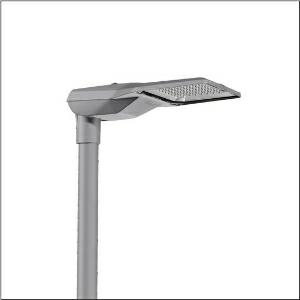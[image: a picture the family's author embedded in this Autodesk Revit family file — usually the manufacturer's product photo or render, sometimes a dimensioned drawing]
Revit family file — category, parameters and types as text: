
# Revit family: streetlight_sl_21_midi___st1_5a_5xe3p33s08mb_c1a7
name_source: partatom
category: Lighting Fixtures
units: mm (PartAtom-declared; Revit-internal decimal feet)

## family parameters
Cut with Voids When Loaded = No
Host = Face
Light Source = No
Part Type = Normal
Room Calculation Point = No
Round Connector Dimension = Use Diameter
Shared = No

## types (1)
- --- (1 x LED, 17960 lm, 136 W, 3000K)
    Apparent Load = 136 VA
    CIE Flux Codes = 22 53 95 100 100
    Color Rendering = 70
    Color Temperature = 3000K
    Default Elevation = 1800 mm
    Description = Streetlight SL 21 midi, mast luminaire, primary light control with lens, of PMMA, primary optical cover: cover, of toughened safety glass, transparent, light distribution: ST1.5a, light emission: direct distribution, primary light characteristic: asymmetric, installation type: side-entry, post-top, LED, High Power LED, rated luminous flux: 17.960lm, luminous efficacy: 132lm/W, light colour: 730, colour temperature: 3000K, control gear: D4i, control: overheat protection, constant luminous flux control, time-dependent luminous flux control, flexible luminous flux parameterisation, pre-setting: logarithmic dimming characteristic, mains connection: 230..240V, AC, 50/60Hz, start of lifetime: 136W, end of service life: 142W, reduction: 61W, luminaire housing, of diecast aluminium, powder-coated, SITECO metallic grey (DB 702S), corrosivity category C5 high according to DIN EN ISO 12944, please order mast flange separately, inclination adjustable: 0°, 5°, 10°, 15°, sealing non-destructively replaceable, multi-level sealing system, length: 644mm, width: 335mm, height: 110mm, mast flange for spigot size: 42mm (side-entry): 5XC10008XM4, 60/48mm (side-entry/post-top): 5XC10108XM2, 76/60mm (side-entry/post-top): 5XC10108XM1, mounting height: 4..8m, Smart Interface above, protection rating (complete): IP66, insulation class (complete): insulation class II (safety insulation), certification: CE, ENEC, ENEC+, VDE, impact resistance: IK10, permissible operating ambient temperature for outdoor applications: -40..+50°C, standard-compliant lighting for roads and squares, packaging unit: 1 piece

Light Distribution: ST1.5a
    Height = 111 mm
    Lamp = 1 x LED
    Lamp Light Flux = 17960 lm
    Lamp Power = 136 W
    Lamp count = 1
    Length = 644 mm
    Luminous efficacy = 132 lm/W
    Manufacturer = Siteco
    ModVariant = No
    Model = 5XE3P33S08MB
    Number of Poles = 1
    OnlyDefault = Yes
    Power Factor = 1
    Product Name = Streetlight SL 21 midi | ST1.5a
    Product group = mast luminaire | pylon top
    ProductGroupID = 6100
    Protection Class = Protection class II
    Protection Degree = IP 66
    RLX_Detail_Level = 1
    RLX_Emergency_Light_Flux = 0 lm
    RLX_Emergency_Type = 0
    RLX_Emergency_Type_DB = No
    RlxData = <blob elided: 30401 chars, md5=7a2e4bdd>
    Socket = socket
    Standby Power = 0 W
    System Light Flux = 17960 lm
    System Power = 136 W
    Type Comments = factory setting: luminous flux: 100 % | dim-lin: 254 | 695 mA
    Type Image = l_1004302.jpg
    URL = http://relux.com
    VarID = @adj_175659
    Voltage = 0 V
    Weight = 0.00 kg
    Width = 336 mm

## geometry (parser evidence)
native form markers: Blend x4, Sweep x11
no freeform markers — native parametric forms only
